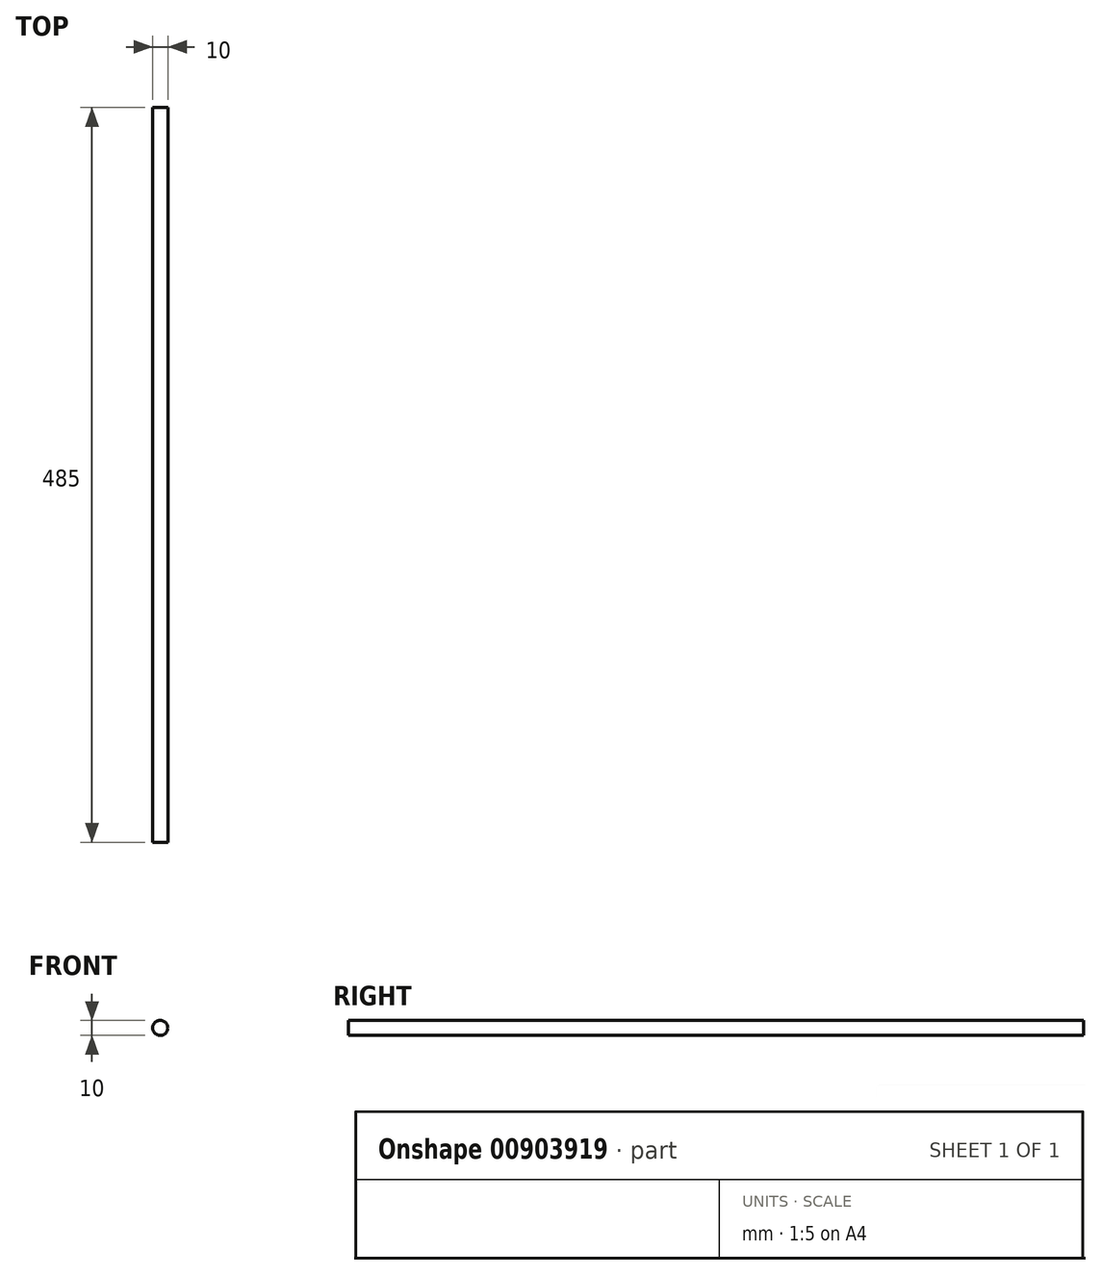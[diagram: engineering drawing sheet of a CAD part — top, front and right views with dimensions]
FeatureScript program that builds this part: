
annotation { "Feature Type Name" : "Feature", "Feature Type Description" : "" }
export const myFeature = defineFeature(function(context is Context, id is Id, definition is map)
    precondition{}
    {
        {
            var Q0;
            Q0=qCreatedBy(makeId("Front.planeOp"),FACE);
            var sketch = newSketch(context, id + "F0", { "sketchPlane" : qUnion([Q0])});
            skCircle(sketch, "E0", {"center": v(0, 0) * mm, "radius": 5 * mm});
            skSolve(sketch);
        }
        {
            var Q0;
            Q0=makeQuery(id+"F0.imprint","IMPRINT",FACE,{"disambiguationData":[TD([[makeQuery(id+"F0.imprint","IMPRINT",EDGE,{"derivedFrom":sQuery(id+"F0.wireOp",EDGE,"E0")}),1.0]])]});
            extrude(context, id + "F1", {"entities" : qUnion([Q0]), "depth" : 495 * mm - 10 * mm, "offsetDistance" : 25 * mm});
        }
    });
